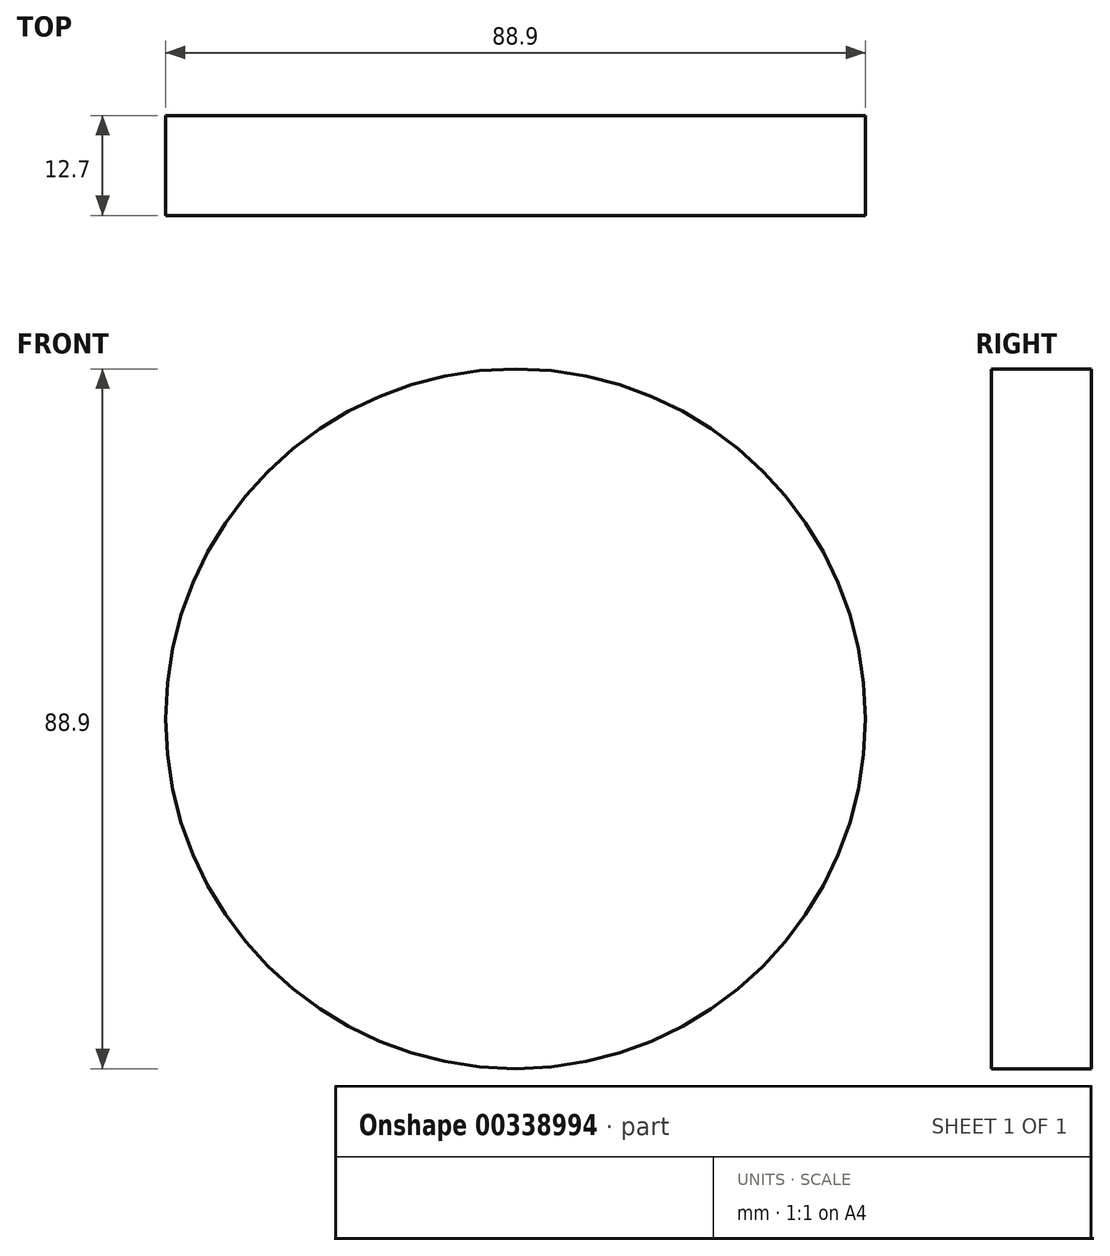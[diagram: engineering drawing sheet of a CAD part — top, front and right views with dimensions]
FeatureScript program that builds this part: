
annotation { "Feature Type Name" : "Feature", "Feature Type Description" : "" }
export const myFeature = defineFeature(function(context is Context, id is Id, definition is map)
    precondition{}
    {
        {
            var Q0;
            Q0=qCreatedBy(makeId("Front.planeOp"),FACE);
            var sketch = newSketch(context, id + "F0", { "sketchPlane" : qUnion([Q0])});
            skCircle(sketch, "E0", {"center": v(0, 0) * mm, "radius": 44.45 * mm});
            skLineSegment(sketch, "E1.bottom", {"start": v(-44.45, 0) * mm, "end": v(45.07, 0) * mm});
            skLineSegment(sketch, "E1.top", {"start": v(-44.45, 26.67) * mm, "end": v(45.07, 26.67) * mm});
            skLineSegment(sketch, "E1.left", {"start": v(-44.45, 0) * mm, "end": v(-44.45, 26.67) * mm});
            skLineSegment(sketch, "E1.right", {"start": v(45.07, 0) * mm, "end": v(45.07, 26.67) * mm});
            skCircle(sketch, "E2.0", {"center": v(0, 0) * mm, "radius": 33.86 * mm});
            skSolve(sketch);
        }
        {
            var Q0;
            Q0=sQuery(id+"F0.wireOp",EDGE,"E0");
            extrude(context, id + "F1", {"bodyType" : ToolBodyType.SURFACE, "surfaceEntities" : qUnion([Q0]), "depth" : 12.7 * mm});
        }
    });
